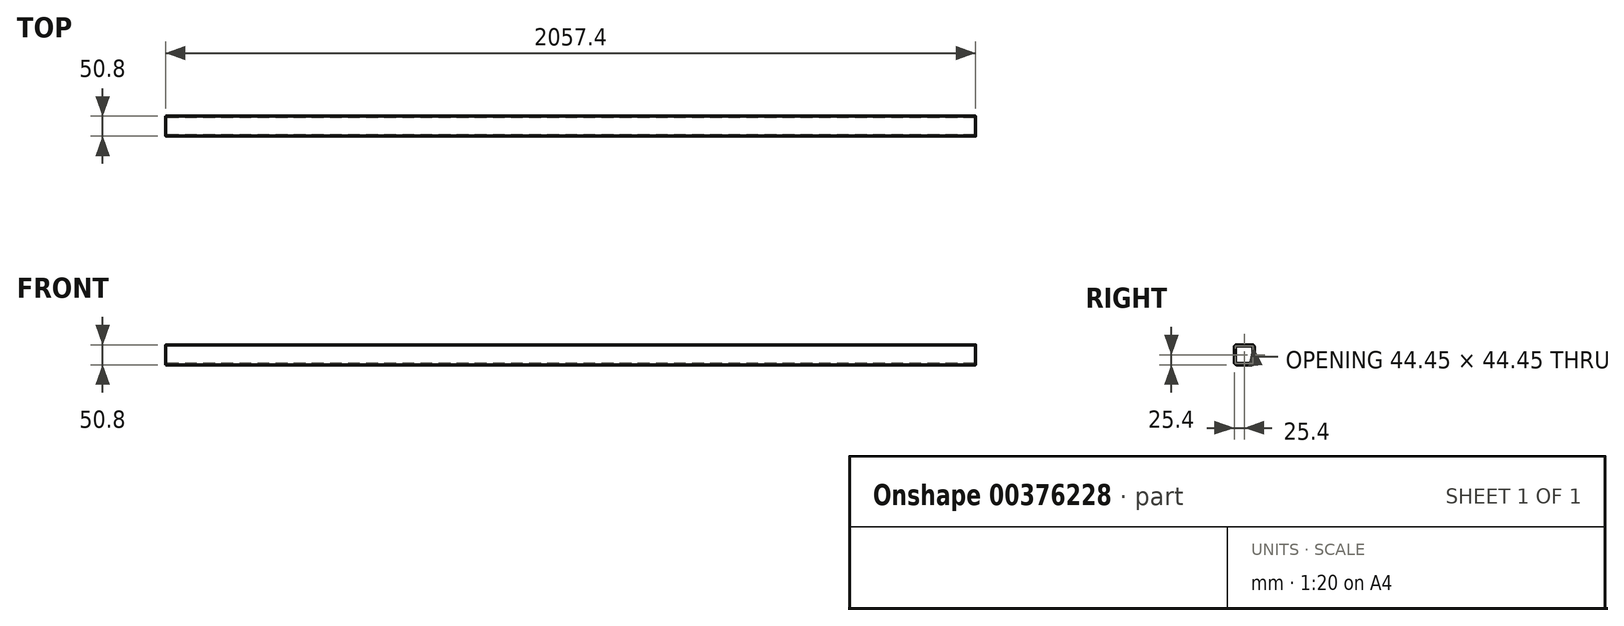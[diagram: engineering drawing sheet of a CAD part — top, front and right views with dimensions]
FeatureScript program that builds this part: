
annotation { "Feature Type Name" : "Feature", "Feature Type Description" : "" }
export const myFeature = defineFeature(function(context is Context, id is Id, definition is map)
    precondition{}
    {
        {
            var Q0;
            Q0=qCreatedBy(makeId("Right.planeOp"),FACE);
            var sketch = newSketch(context, id + "F0", { "sketchPlane" : qUnion([Q0])});
            skLineSegment(sketch, "E0.bottom", {"start": v(19.05, 25.4) * mm, "end": v(-19.05, 25.4) * mm});
            skLineSegment(sketch, "E0.top", {"start": v(19.05, -25.4) * mm, "end": v(-19.05, -25.4) * mm});
            skLineSegment(sketch, "E0.left", {"start": v(25.4, 19.05) * mm, "end": v(25.4, -19.05) * mm});
            skLineSegment(sketch, "E0.right", {"start": v(-25.4, 19.05) * mm, "end": v(-25.4, -19.05) * mm});
            skPoint(sketch, "E0.middle", {"position": v(0, 0) * mm});
            skPoint(sketch, "E1.visualSharp", {"position": v(-25.4, 25.4) * mm});
            skArc(sketch, "E1.filletArc", {"start": v(-19.05, 25.4) * mm, "mid": v(-23.54, 23.54) * mm, "end": v(-25.4, 19.05) * mm});
            skPoint(sketch, "E2.visualSharp", {"position": v(25.4, 25.4) * mm});
            skArc(sketch, "E2.filletArc", {"start": v(25.4, 19.05) * mm, "mid": v(23.54, 23.54) * mm, "end": v(19.05, 25.4) * mm});
            skPoint(sketch, "E3.visualSharp", {"position": v(25.4, -25.4) * mm});
            skArc(sketch, "E3.filletArc", {"start": v(19.05, -25.4) * mm, "mid": v(23.54, -23.54) * mm, "end": v(25.4, -19.05) * mm});
            skPoint(sketch, "E4.visualSharp", {"position": v(-25.4, -25.4) * mm});
            skArc(sketch, "E4.filletArc", {"start": v(-25.4, -19.05) * mm, "mid": v(-23.54, -23.54) * mm, "end": v(-19.05, -25.4) * mm});
            skArc(sketch, "E5.0", {"start": v(22.23, 19.05) * mm, "mid": v(21.3, 21.3) * mm, "end": v(19.05, 22.23) * mm});
            skLineSegment(sketch, "E5.1", {"start": v(22.23, 19.05) * mm, "end": v(22.23, -19.05) * mm});
            skLineSegment(sketch, "E5.2", {"start": v(19.05, 22.23) * mm, "end": v(-19.05, 22.23) * mm});
            skArc(sketch, "E5.3", {"start": v(19.05, -22.23) * mm, "mid": v(21.3, -21.3) * mm, "end": v(22.23, -19.05) * mm});
            skArc(sketch, "E5.4", {"start": v(-19.05, 22.23) * mm, "mid": v(-21.3, 21.3) * mm, "end": v(-22.23, 19.05) * mm});
            skLineSegment(sketch, "E5.5", {"start": v(-22.23, 19.05) * mm, "end": v(-22.23, -19.05) * mm});
            skArc(sketch, "E5.6", {"start": v(-22.23, -19.05) * mm, "mid": v(-21.3, -21.3) * mm, "end": v(-19.05, -22.23) * mm});
            skLineSegment(sketch, "E5.7", {"start": v(19.05, -22.23) * mm, "end": v(-19.05, -22.23) * mm});
            skSolve(sketch);
        }
        {
            var Q0;
            Q0 = qSketchRegion(id + "F0", true);
            extrude(context, id + "F1", {"entities" : qUnion([Q0]), "oppositeDirection" : true, "depth" : -2057.4 * mm});
        }
    });
